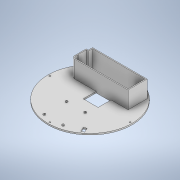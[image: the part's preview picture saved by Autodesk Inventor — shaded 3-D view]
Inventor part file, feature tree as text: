
AUTODESK INVENTOR PART (.ipt)
format: ipt  version: 2021 (Build 250183000, 183)  size: 198,656 bytes
history: native  units: mm
features: extrude x7, other x2, hole x1, pattern_circular x1
ambient origin geometry x8: Origin, YZ Plane, XZ Plane, XY Plane, X Axis, Y Axis, Z Axis, Center Point
bodies: Volumenkörper1 (feature_tree)
feature tree (11):
  other  "00_Mastersketch.ipt"
  extrude  "Extrusion1"  Depth=10.0mm
  extrude  "Extrusion2"  Depth=3.6mm TaperAngle=0.0deg
  hole  "Bohrung1"  [1 undecoded]
  pattern_circular  "Runde Anordnung1"  [2 undecoded]
  extrude  "Extrusion5"  Depth=40.0mm TaperAngle=360.0deg
  extrude  "Extrusion6"  Depth=0.1mm
  extrude  "Extrusion7"  TaperAngle=0.0deg  [1 undecoded]
  extrude  "Extrusion8"  Depth=1.6mm TaperAngle=0.0deg
  extrude  "Extrusion9"  TaperAngle=0.0deg  [1 undecoded]
  other  "03_caseTopSketch"
note: 5 required parameter values undecoded (feature->parameter linkage not recoverable at this tier; creation-order binding heuristic only, values carry confidence <= 0.55)
